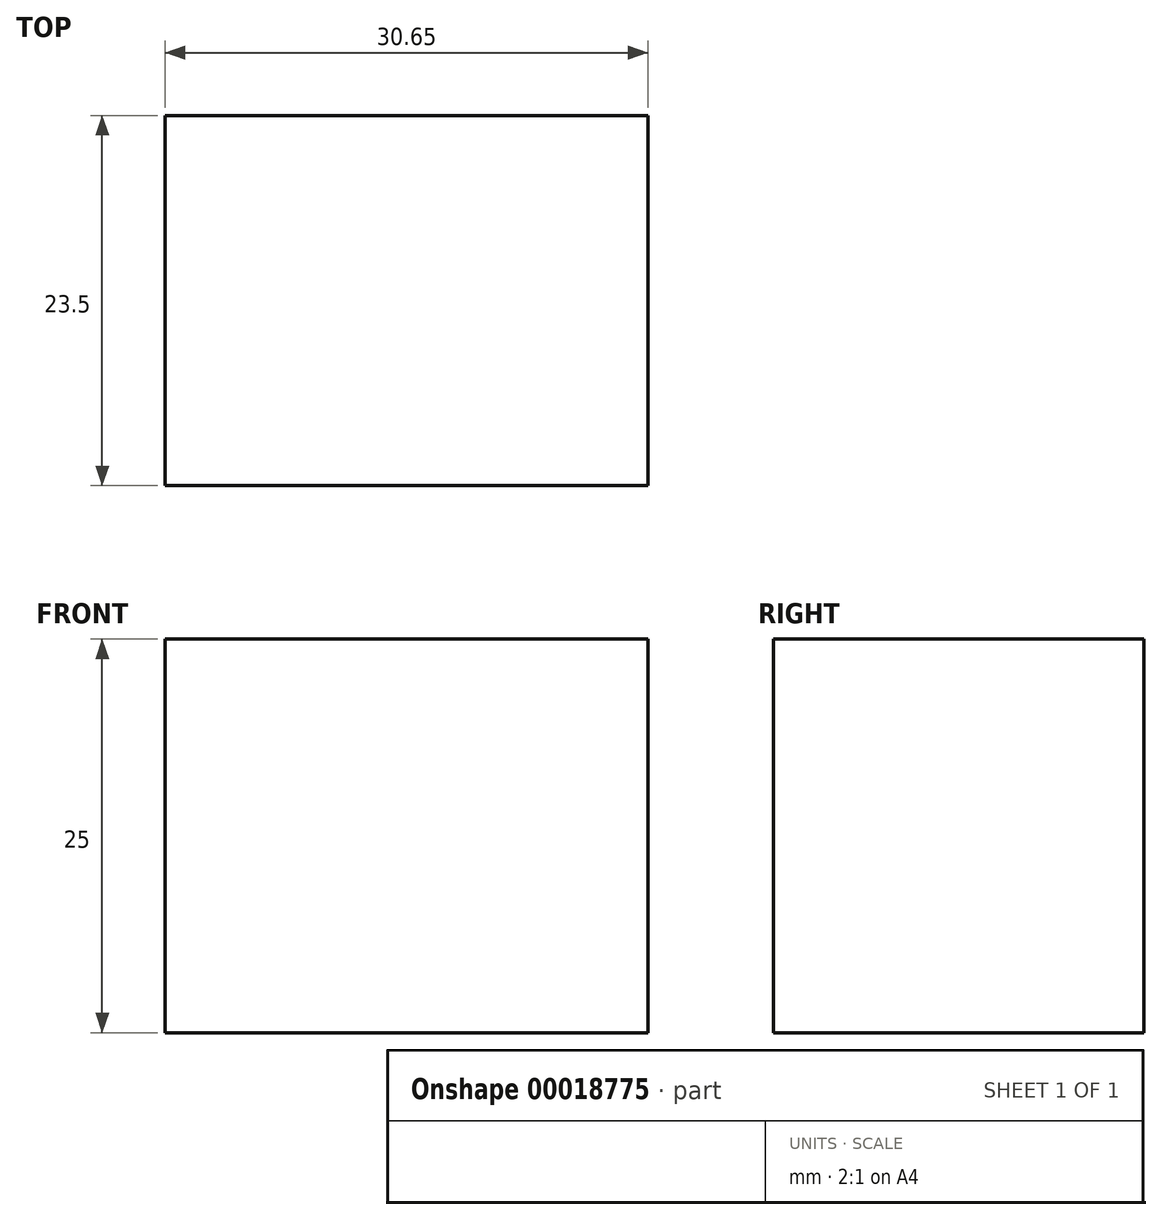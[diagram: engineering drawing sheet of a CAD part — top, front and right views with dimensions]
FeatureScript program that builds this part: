
annotation { "Feature Type Name" : "Feature", "Feature Type Description" : "" }
export const myFeature = defineFeature(function(context is Context, id is Id, definition is map)
    precondition{}
    {
        {
            var Q0;
            Q0=qCreatedBy(makeId("Top.planeOp"),FACE);
            var sketch = newSketch(context, id + "F0", { "sketchPlane" : qUnion([Q0])});
            skLineSegment(sketch, "E0.bottom", {"start": v(0, 0) * mm, "end": v(30.65, 0) * mm});
            skLineSegment(sketch, "E0.top", {"start": v(0, -23.5) * mm, "end": v(30.65, -23.5) * mm});
            skLineSegment(sketch, "E0.left", {"start": v(0, 0) * mm, "end": v(0, -23.5) * mm});
            skLineSegment(sketch, "E0.right", {"start": v(30.65, 0) * mm, "end": v(30.65, -23.5) * mm});
            skSolve(sketch);
        }
        {
            var Q0;
            Q0=makeQuery(id+"F0.imprint","IMPRINT",FACE,{"disambiguationData":[TD([[makeQuery(id+"F0.imprint","IMPRINT",EDGE,{"derivedFrom":sQuery(id+"F0.wireOp",EDGE,"E0.bottom")}),-1.0]])]});
            extrude(context, id + "F1", {"entities" : qUnion([Q0]), "depth" : 25 * mm});
        }
    });
